# Revit family: Lighting_Pendant-Lighting_Molto-Luce_Dark-Night-XS-Volare_999
name_source: partatom
category: Lighting Fixtures
revit_build: Autodesk Revit 2018 (Build: 20170223_1515(x64)
units: mm (PartAtom-declared; Revit-internal decimal feet)

## family parameters
Cut with Voids When Loaded = No
Host = Face
Light Source = Yes
OmniClass Number = 23.80.70.00
OmniClass Title = Lighting
Part Type = Normal
Room Calculation Point = No
Round Connector Dimension = Use Diameter
Shared = No

## types (1)
- Default - please load Revit Family Type Catalog
    BIMobject category = Pendant Lighting
    Color Filter = 16777215
    Decor Color = Molto Luce - Gold
    Default Elevation = 1219 mm
    Description = The varied product family DARK NIGHT impresses with its adaptability, from downlight and swivelling downlight to pendant luminaire with canopy or VOLARE adapter through to surface mounted downlight - DARK NIGHT can do it all. DARK NIGHT LGP is a special highlight, which stands out with the option of emitting either directed light or diffuse light via the Light Guide Pipe. The possibility of mixing diffuse and directed light opens up completely new possibilities to stage rooms differently. The DARK NIGHT family is available in black and white powder-coated housings and reflectors in high-gloss black, matt silver, white and gold.
The possibility of mixing diffuse and directed light opens up completely new possibilities to stage rooms differently. The luminaire which combines sophisticated technology and high design standards creates diverse light atmospheres.
SPOT LIGHT ON
The directed light of the Dark Night LGP stages only selected areas. Individual accents cleverly draw attention to the main aspects of the room.
AREA LIGHT ON
The diffuse light of the Light Guide Pipe gives every room an individual and special atmosphere. The soft and gentle light creates different emotions.
SPOT + AREA LIGHT ON
The combination of directed light and diffuse light allows for an almost endless variety of different light atmosphere presentations. The broad range of applications of the Dark Night LGP offers new ways to adapt the room to personal needs. 
Light Guide Pipe
The Light Guide Pipe technology are thousands of microscopically small laser-drilled holes in the luminaire's external cover which spread the LED light horizontally in the room. The light can be dimmed smoothly to create every kind of mood.
Glare-free visual comfort
In combination with the coloured decorative elements, the recessed reflector provides for direct light without glare.
Controlling
The Dark Night LGP can be perfectly adapted to the controlling technology required by the object. CASAMBI, DALI and ZIGBEE are some possibilities for adaption. On top of that, the 'Molto Luce Smart App' ensures an especially simple and comfortable operation via smartphone or tablet.
Applications
The Dark Night LGP creates individual lighting concepts for a variety of applications. The surface luminaire offers not only targeted and scattered light, but it is also switchable and dimmable, which makes it a unique illumination system for hotels and restaurants as well as the private sphere.
The Dark Night LGP is available with black and white powder-coated housings and with reflectors in high-gloss black, matt silver, white and gold. The combination of individual elements of the luminaire in different colours allows for a variety of designs and perfect integration into the room characteristic.
    Design country = Austria
    Dimming Lamp Color Temperature Shift = <None>
    Edition number = 1
    Housing Color = Molto Luce - Black
    IFC Classification = Lamp
    Light Source Symbol Length = 1500 mm  [stored 4.92126 ft]
    Manufacturer = Molto Luce
    Manufacturer country = Austria
    Manufacturer name = Molto Luce
    Masterformat 2014 Code = 26 50 00
    Masterformat 2014 Description = Lighting
    Material main = Aluminium
    Model = Dark Night XS Volare
    NBS Reference Code = 49
    NBS Reference Description = Luminaires And Lamps
    OmniClass Code = 23-35 45 15
    OmniClass Description = Lamps
    Product Guid = c3dc6662-7dfc-4745-940d-48684bf93258
    Product SKU = Dark_Night_XS_Volare
    Product data url = https://bimobject.com
    Product family = Lighting
    Product group = Pendant Lamp
    Product name = Dark Night XS Volare
    QR code = https://bimobject.com
    Spot Beam Angle = 30.00°
    Spot Field Angle = 90.00°
    Tilt Angle = 90.00°
    UNSPSC Code = 3911
    URL = https://www.moltoluce.com
    Uniclass 1.4 Code = JY73
    Uniclass 1.4 Description = Luminaires and lamps
    Uniclass 2.0 Code = PR-49
    Uniclass 2.0 Description = Luminaires And Lamps
    Uniclass 2015 Code = Pr_70_70_48
    Uniclass 2015 Name = Luminaires, lighting track and lighting accessories
    Uniformat II Code = D5020
    Uniformat II Description = Lighting & Branch Wiring

note: [stored X ft] marks values corroborated as IEEE doubles in the binary element streams (Revit-internal decimal feet)

## geometry (parser evidence)
native form markers: Sweep x27
no freeform markers — native parametric forms only
